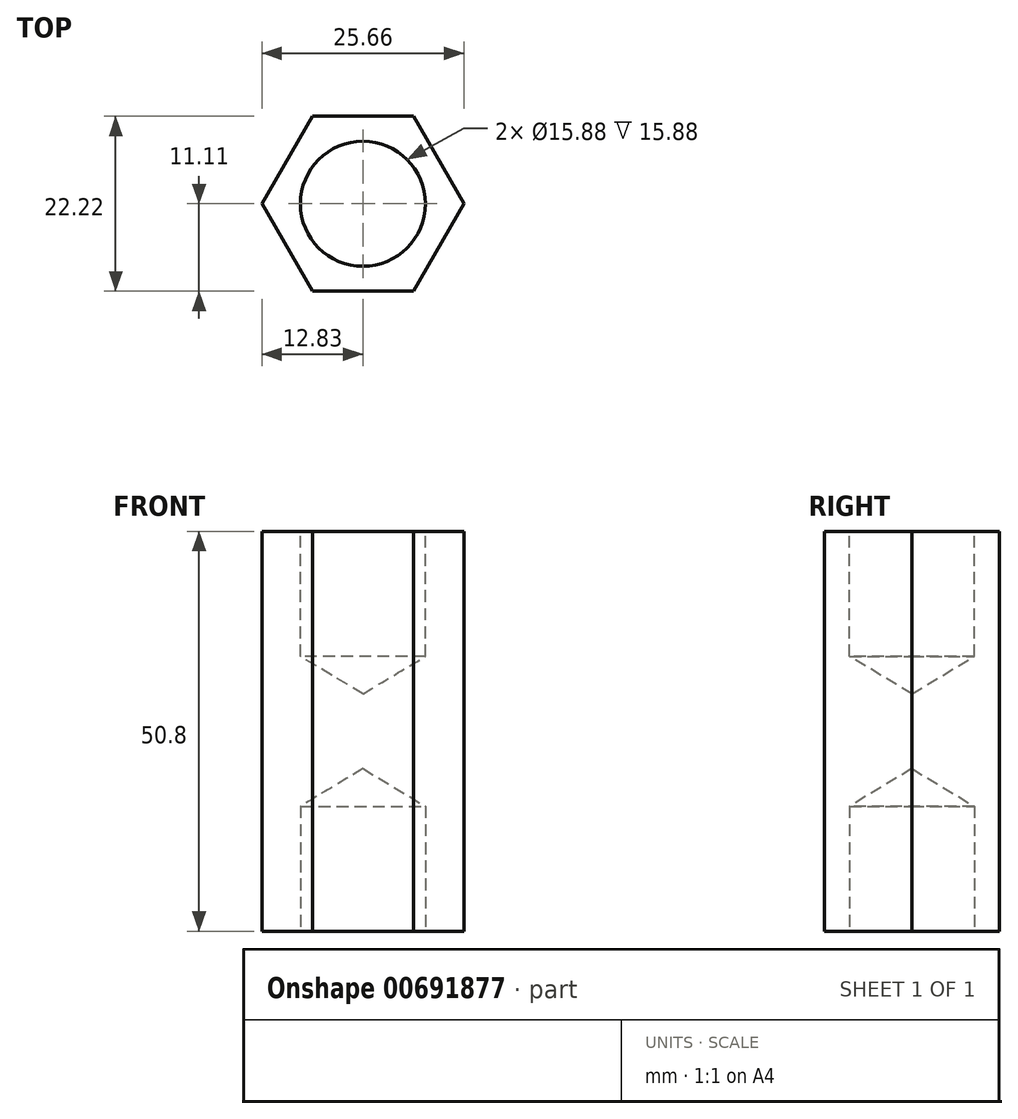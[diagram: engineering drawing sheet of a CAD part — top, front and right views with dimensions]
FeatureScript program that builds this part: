
annotation { "Feature Type Name" : "Feature", "Feature Type Description" : "" }
export const myFeature = defineFeature(function(context is Context, id is Id, definition is map)
    precondition{}
    {
        {
            var Q0;
            Q0=qCreatedBy(makeId("Top.planeOp"),FACE);
            var sketch = newSketch(context, id + "F0", { "sketchPlane" : qUnion([Q0])});
            skCircle(sketch, "E0", {"center": v(0, 0) * mm, "radius": 11.11 * mm, "construction": true});
            skLineSegment(sketch, "E1.0", {"start": v(-6.42, 11.11) * mm, "end": v(6.42, 11.11) * mm});
            skLineSegment(sketch, "E1.1", {"start": v(6.42, 11.11) * mm, "end": v(12.83, 0) * mm});
            skLineSegment(sketch, "E1.2", {"start": v(12.83, 0) * mm, "end": v(6.42, -11.11) * mm});
            skLineSegment(sketch, "E1.3", {"start": v(6.42, -11.11) * mm, "end": v(-6.42, -11.11) * mm});
            skLineSegment(sketch, "E1.4", {"start": v(-6.42, -11.11) * mm, "end": v(-12.83, 0) * mm});
            skLineSegment(sketch, "E1.5", {"start": v(-12.83, 0) * mm, "end": v(-6.42, 11.11) * mm});
            skPoint(sketch, "E1.0.midPoint", {"position": v(0, 11.11) * mm});
            skSolve(sketch);
        }
        {
            var Q0;
            Q0 = qSketchRegion(id + "F0", true);
            extrude(context, id + "F1", {"entities" : qUnion([Q0]), "depth" : 50.8 * mm, "offsetDistance" : 25.4 * mm});
        }
        {
            var Q0;
            Q0=sQuery(id+"F0.wireOp",VERTEX,"E0.center");
            var Q1;
            Q1=makeQuery(id+"F1.opExtrude","SWEPT_BODY",BODY,{"disambiguationData":[OSD([sQuery(id+"F0.wireOp",EDGE,"E1.0"),sQuery(id+"F0.wireOp",EDGE,"E1.1"),sQuery(id+"F0.wireOp",EDGE,"E1.2"),sQuery(id+"F0.wireOp",EDGE,"E1.3"),sQuery(id+"F0.wireOp",EDGE,"E1.4"),sQuery(id+"F0.wireOp",EDGE,"E1.5")])]});
            hole(context, id + "F2", {"style" : HoleStyle.SIMPLE, "endStyle" : HoleEndStyle.BLIND, "oppositeDirection" : true, "holeDiameter" : 15.88 * mm, "majorDiameter" : 6.35 * mm, "holeDepth" : 15.88 * mm, "isTappedThrough" : true, "tappedDepth" : 12.7 * mm, "tapClearance" : 3, "locations" : qUnion([Q0]), "scope" : qUnion([Q1])});
        }
        {
            var Q0;
            Q0=makeQuery(id+"F1.opExtrude","CAP_FACE",FACE,{"disambiguationData":[OSD([sQuery(id+"F0.wireOp",EDGE,"E1.0"),sQuery(id+"F0.wireOp",EDGE,"E1.1"),sQuery(id+"F0.wireOp",EDGE,"E1.2"),sQuery(id+"F0.wireOp",EDGE,"E1.3"),sQuery(id+"F0.wireOp",EDGE,"E1.4"),sQuery(id+"F0.wireOp",EDGE,"E1.5")])],"isStart":false});
            var sketch = newSketch(context, id + "F3", { "sketchPlane" : qUnion([Q0])});
            skCircle(sketch, "E2", {"center": v(0, 0) * mm, "radius": 11.11 * mm});
            skSolve(sketch);
        }
        {
            var Q0;
            Q0=sQuery(id+"F3.wireOp",VERTEX,"E2.center");
            var Q1;
            Q1=makeQuery(id+"F1.opExtrude","SWEPT_BODY",BODY,{"disambiguationData":[OSD([sQuery(id+"F0.wireOp",EDGE,"E1.0"),sQuery(id+"F0.wireOp",EDGE,"E1.1"),sQuery(id+"F0.wireOp",EDGE,"E1.2"),sQuery(id+"F0.wireOp",EDGE,"E1.3"),sQuery(id+"F0.wireOp",EDGE,"E1.4"),sQuery(id+"F0.wireOp",EDGE,"E1.5")])]});
            hole(context, id + "F4", {"style" : HoleStyle.SIMPLE, "endStyle" : HoleEndStyle.BLIND, "holeDiameter" : 15.88 * mm, "majorDiameter" : 6.35 * mm, "holeDepth" : 15.88 * mm, "isTappedThrough" : true, "tappedDepth" : 12.7 * mm, "tapClearance" : 3, "locations" : qUnion([Q0]), "scope" : qUnion([Q1])});
        }
    });
